# Revit family: NBS_WallgateLtd_Mrrs_ALM
name_source: partatom
category: Specialty Equipment
revit_build: Autodesk Revit 2014 (Build: 20130709_2115(x64)
units: mm (PartAtom-declared; Revit-internal decimal feet)

## types (2) — shared parameters
AssetType = Fixed
Certification = Ministry of Justice Safer Cell Approval
ColourOptions = MA - Thames, MAH - Frost, MAW - White, MC - Bluestone, MCA - Aubergine, MCB - Diamantina, MCC - Black, MCD - Orange, MCE - Pink, MO - Slate, MS - Hyco, MCJ - Light Grey, MCF - NHS Blue
Description = Anti-ligature, anti-vandal polycarbonate mirror with solid surface surround
Durability = Compliant to Grade 5
DurationUnit = year
Features = Hygienic and easily cleaned, highly vandal-resistant
Finish = Solid Surface
FormOptions = Wall mounted or security screws
IfcExportAs = IfcFurnitureType
IfcExportType = MIRROR
ManufacturerName = Wallgate Ltd
ManufacturerURL = www.wallgate.com
MaterialFrame = High-grade solid surface material
MaterialGlazing = Scratch Resistant Polycarbonate, backed with 6 mm MDF
MirrorDepth = 20 mm  [stored 0.0656168 ft]
MirrorFrameMaterial = NBS_Concept
MirrorMaterial = NBS_Concept
NBSCertification = www.nationalbimlibrary.com/cert/24nxz44n
NBSDescription = Mirrors
NBSReference = 45-35-72/336
NominalDepth = 20 mm  [stored 0.0656168 ft]
ProductInformation = www.wallgate.com/products/washroom-accessories/alm-anti-ligature-mirrors-range
Shape = Rectangular
Uniclass2 = 45-71-53/406
Version = 1
WarrantyDurationParts = 1
WarrantyDurationUnit = year
zero-valued in all types: NominalLength

## per-type parameters (varying)
| type | BIMObjectName | MirrorHeight | MirrorWidth | Name | NominalHeight | NominalWidth | Size | Weight |
| ALM-02 | NBS_WallgateLtd_Mirrors_ALM-02 | 350 mm  [stored 1.14829 ft] | 250 mm  [stored 0.82021 ft] | Mirrors_ALM-02_WallgateLtd | 350 mm  [stored 1.14829 ft] | 250 mm  [stored 0.82021 ft] | 350 x 250 x 20 mm | 1.6 kg |
| ALM-03 | NBS_WallgateLtd_Mirrors_ALM-03 | 650 mm | 500 mm  [stored 1.64042 ft] | Mirrors_ALM-03_WallgateLtd | 650 mm | 500 mm  [stored 1.64042 ft] | 650 x 500 x 20 mm | 4.0 kg |

note: column(s) folded — value = type name in every type: ModelNumber

note: [stored X ft] marks values corroborated as IEEE doubles in the binary element streams (Revit-internal decimal feet)

## geometry (parser evidence)
native form markers: Sweep x1
no freeform markers — native parametric forms only
